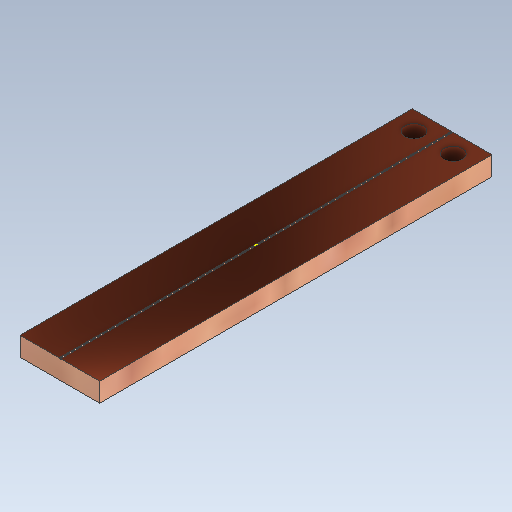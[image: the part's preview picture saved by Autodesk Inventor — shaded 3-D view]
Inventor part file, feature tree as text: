
AUTODESK INVENTOR PART (.ipt)
format: ipt  version: 2021 (Build 250183000, 183)  size: 131,584 bytes
history: native  units: in
note: dims shown in document units (in); Inventor stores cm internally (conversion verified against a paired STEP export)
features: sketch x4, other x3
ambient origin geometry x8: Origin, YZ Plane, XZ Plane, XY Plane, X Axis, Y Axis, Z Axis, Center Point
bodies: Solid1 (feature_tree)
feature tree (7):
  other  "Leads+ChannelForSingleHeater.ipt"
  other  "Solid1::Leads+ChannelForSingleHeater.ipt"
  other  "TaggingFeature1"
  sketch  "Sketch1"  dims[d0=0.3937in]
  sketch  "Sketch2"  dims[d1=0.12in]
  sketch  "Sketch3"
  sketch  "Sketch4"
